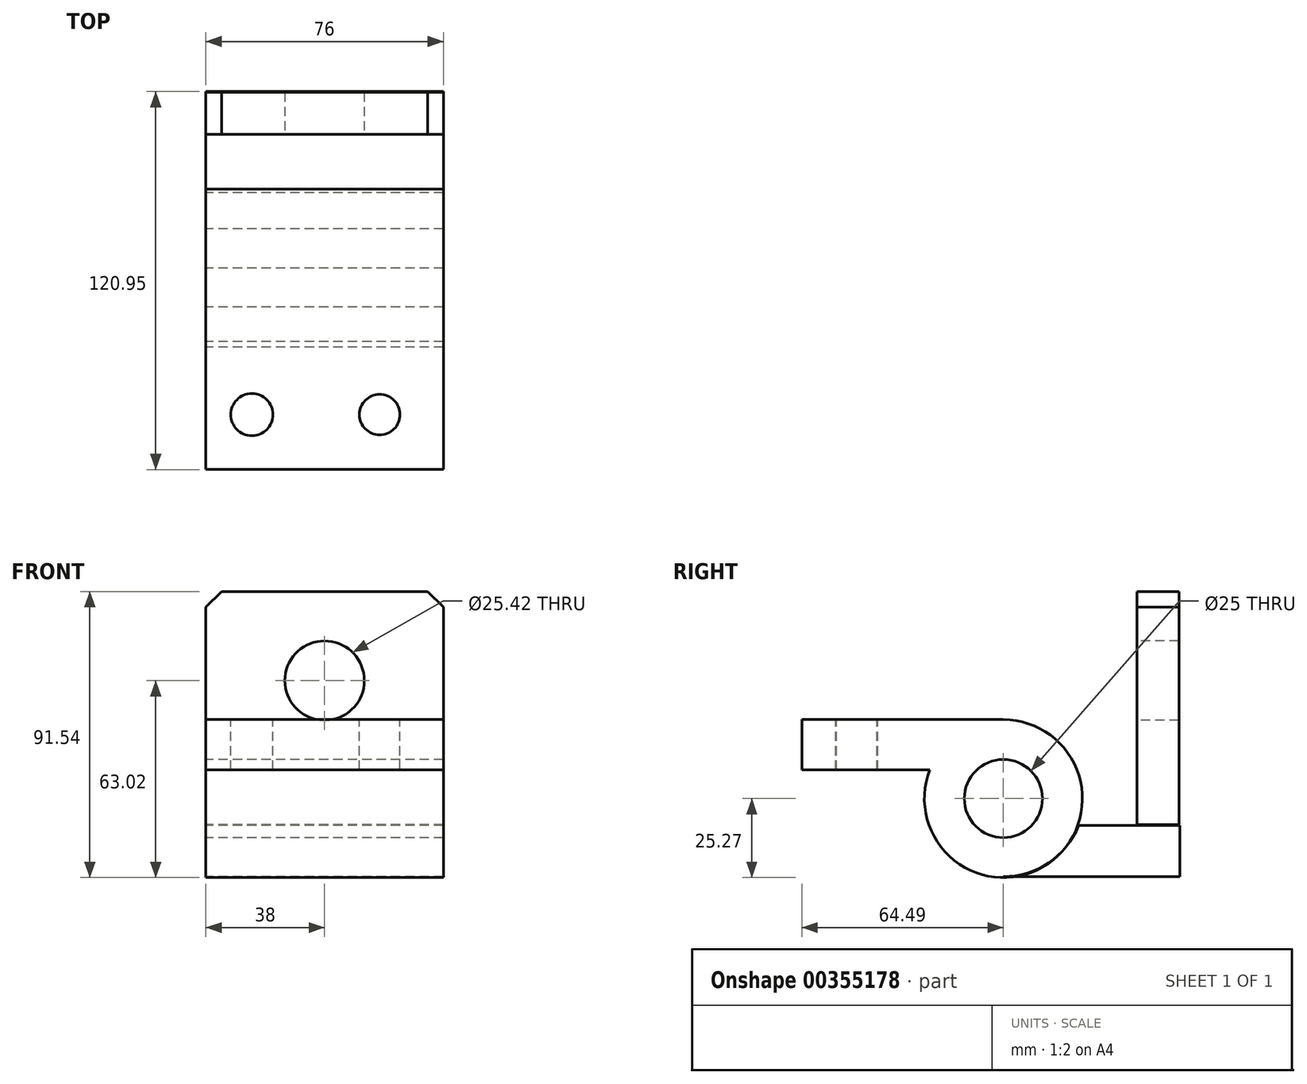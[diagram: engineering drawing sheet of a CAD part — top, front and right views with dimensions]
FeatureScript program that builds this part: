
annotation { "Feature Type Name" : "Feature", "Feature Type Description" : "" }
export const myFeature = defineFeature(function(context is Context, id is Id, definition is map)
    precondition{}
    {
        {
            var Q0;
            Q0=qCreatedBy(makeId("Right.planeOp"),FACE);
            var sketch = newSketch(context, id + "F0", { "sketchPlane" : qUnion([Q0])});
            skCircle(sketch, "E0", {"center": v(0, 0) * mm, "radius": 12.5 * mm});
            skSolve(sketch);
        }
        {
            var Q0;
            Q0=qCreatedBy(makeId("Right.planeOp"),FACE);
            var sketch = newSketch(context, id + "F1", { "sketchPlane" : qUnion([Q0])});
            skCircle(sketch, "E1", {"center": v(0, 0) * mm, "radius": 25.27 * mm});
            skLineSegment(sketch, "E2", {"start": v(0, 25.27) * mm, "end": v(-64.49, 25.27) * mm});
            skLineSegment(sketch, "E3", {"start": v(-64.49, 25.27) * mm, "end": v(-64.49, 9.21) * mm});
            skLineSegment(sketch, "E4", {"start": v(-64.49, 9.21) * mm, "end": v(-23.54, 9.21) * mm});
            skSolve(sketch);
        }
        {
            var Q0;
            Q0=qCreatedBy(makeId("Right.planeOp"),FACE);
            var sketch = newSketch(context, id + "F2", { "sketchPlane" : qUnion([Q0])});
            skLineSegment(sketch, "E5", {"start": v(0, -24.96) * mm, "end": v(56.46, -24.96) * mm});
            skLineSegment(sketch, "E6", {"start": v(56.46, -24.96) * mm, "end": v(56.46, -8.62) * mm});
            skLineSegment(sketch, "E7", {"start": v(56.46, -8.62) * mm, "end": v(24.07, -8.62) * mm});
            skArc(sketch, "E8", {"start": v(0, -24.96) * mm, "mid": v(14.55, -20.5) * mm, "end": v(24.07, -8.62) * mm});
            skSolve(sketch);
        }
        {
            var Q0;
            Q0=qCreatedBy(makeId("Right.planeOp"),FACE);
            var sketch = newSketch(context, id + "F3", { "sketchPlane" : qUnion([Q0])});
            skLineSegment(sketch, "E9", {"start": v(42.8, -8.32) * mm, "end": v(56.17, -8.32) * mm});
            skLineSegment(sketch, "E10", {"start": v(42.8, -8.32) * mm, "end": v(42.8, 66.27) * mm});
            skLineSegment(sketch, "E11", {"start": v(56.17, -8.32) * mm, "end": v(56.17, 66.27) * mm});
            skLineSegment(sketch, "E12", {"start": v(56.17, 66.27) * mm, "end": v(42.8, 66.27) * mm});
            skSolve(sketch);
        }
        {
            var Q0;
            {var subQ0=sQuery(id+"F1.wireOp",EDGE,"E2");Q0=makeQuery(id+"F1.imprint","IMPRINT",FACE,{"disambiguationData":[TD([[makeQuery(id+"F1.imprint","IMPRINT",EDGE,{"derivedFrom":subQ0}),1.0]])]});}
            var Q1;
            {var subQ0=sQuery(id+"F1.wireOp",EDGE,"E1");var subQ1=makeQuery(id+"F1.imprint","INTERSECT",VERTEX,{"derivedFrom":[subQ0,sQuery(id+"F1.wireOp",EDGE,"E2")]});Q1=makeQuery(id+"F1.imprint","IMPRINT",FACE,{"disambiguationData":[TD([[makeQuery(id+"F1.imprint","IMPRINT",EDGE,{"disambiguationData":[TD([[subQ1,-1.0]])],"derivedFrom":subQ0}),1.0]])]});}
            var Q2;
            Q2=makeQuery(id+"F2.imprint","IMPRINT",FACE,{"disambiguationData":[TD([[makeQuery(id+"F2.imprint","IMPRINT",EDGE,{"derivedFrom":sQuery(id+"F2.wireOp",EDGE,"E5")}),1.0]])]});
            var Q3;
            Q3=makeQuery(id+"F3.imprint","IMPRINT",FACE,{"disambiguationData":[TD([[makeQuery(id+"F3.imprint","IMPRINT",EDGE,{"derivedFrom":sQuery(id+"F3.wireOp",EDGE,"E9")}),1.0]])]});
            extrude(context, id + "F4", {"entities" : qUnion([Q0, Q1, Q2, Q3]), "depth" : 76 * mm});
        }
        {
            var Q0;
            Q0=makeQuery(id+"F4.opExtrude","CAP_EDGE",EDGE,{"disambiguationData":[OSD([sQuery(id+"F3.wireOp",EDGE,"E12")])],"isStart":false});
            var Q1;
            Q1=makeQuery(id+"F4.opExtrude","CAP_EDGE",EDGE,{"disambiguationData":[OSD([sQuery(id+"F3.wireOp",EDGE,"E12")])],"isStart":true});
            chamfer(context, id + "F5", {"entities" : qUnion([Q0, Q1]), "width" : 5 * mm, "tangentPropagation" : true});
        }
        {
            var Q0;
            Q0=makeQuery(id+"F0.imprint","IMPRINT",FACE,{"disambiguationData":[TD([[makeQuery(id+"F0.imprint","IMPRINT",EDGE,{"derivedFrom":sQuery(id+"F0.wireOp",EDGE,"E0")}),1.0]])]});
            extrude(context, id + "F6", {"entities" : qUnion([Q0]), "operationType" : NewBodyOperationType.REMOVE, "depth" : 113 * mm});
        }
        {
            var Q0;
            Q0=makeQuery(id+"F4.opExtrude","SWEPT_FACE",FACE,{"disambiguationData":[OSD([sQuery(id+"F3.wireOp",EDGE,"E10")])]});
            var sketch = newSketch(context, id + "F7", { "sketchPlane" : qUnion([Q0])});
            skCircle(sketch, "E13", {"center": v(38, 37.75) * mm, "radius": 12.7 * mm});
            skPoint(sketch, "E13.centerSnap0", {"position": v(38, 66.27) * mm});
            skSolve(sketch);
        }
        {
            var Q0;
            Q0=makeQuery(id+"F7.imprint","IMPRINT",FACE,{"disambiguationData":[TD([[makeQuery(id+"F7.imprint","IMPRINT",EDGE,{"derivedFrom":sQuery(id+"F7.wireOp",EDGE,"E13")}),1.0]])]});
            var Q1;
            Q1=sQuery(id+"F7.wireOp",EDGE,"E13");
            extrude(context, id + "F8", {"entities" : qUnion([Q0]), "operationType" : NewBodyOperationType.REMOVE, "surfaceEntities" : qUnion([Q1]), "oppositeDirection" : true, "depth" : 25 * mm});
        }
        {
            var Q0;
            Q0=makeQuery(id+"F4.opExtrude","SWEPT_FACE",FACE,{"disambiguationData":[OSD([sQuery(id+"F1.wireOp",EDGE,"E2")])]});
            var sketch = newSketch(context, id + "F9", { "sketchPlane" : qUnion([Q0])});
            skCircle(sketch, "E14", {"center": v(14.72, -46.9) * mm, "radius": 6.73 * mm});
            skCircle(sketch, "E15", {"center": v(55.63, -46.9) * mm, "radius": 6.49 * mm});
            skSolve(sketch);
        }
        {
            var Q0;
            Q0=makeQuery(id+"F9.imprint","IMPRINT",FACE,{"disambiguationData":[TD([[makeQuery(id+"F9.imprint","IMPRINT",EDGE,{"derivedFrom":sQuery(id+"F9.wireOp",EDGE,"E14")}),1.0]])]});
            var Q1;
            Q1=makeQuery(id+"F9.imprint","IMPRINT",FACE,{"disambiguationData":[TD([[makeQuery(id+"F9.imprint","IMPRINT",EDGE,{"derivedFrom":sQuery(id+"F9.wireOp",EDGE,"E15")}),1.0]])]});
            extrude(context, id + "F10", {"entities" : qUnion([Q0, Q1]), "operationType" : NewBodyOperationType.REMOVE, "oppositeDirection" : true, "depth" : 25 * mm});
        }
    });
